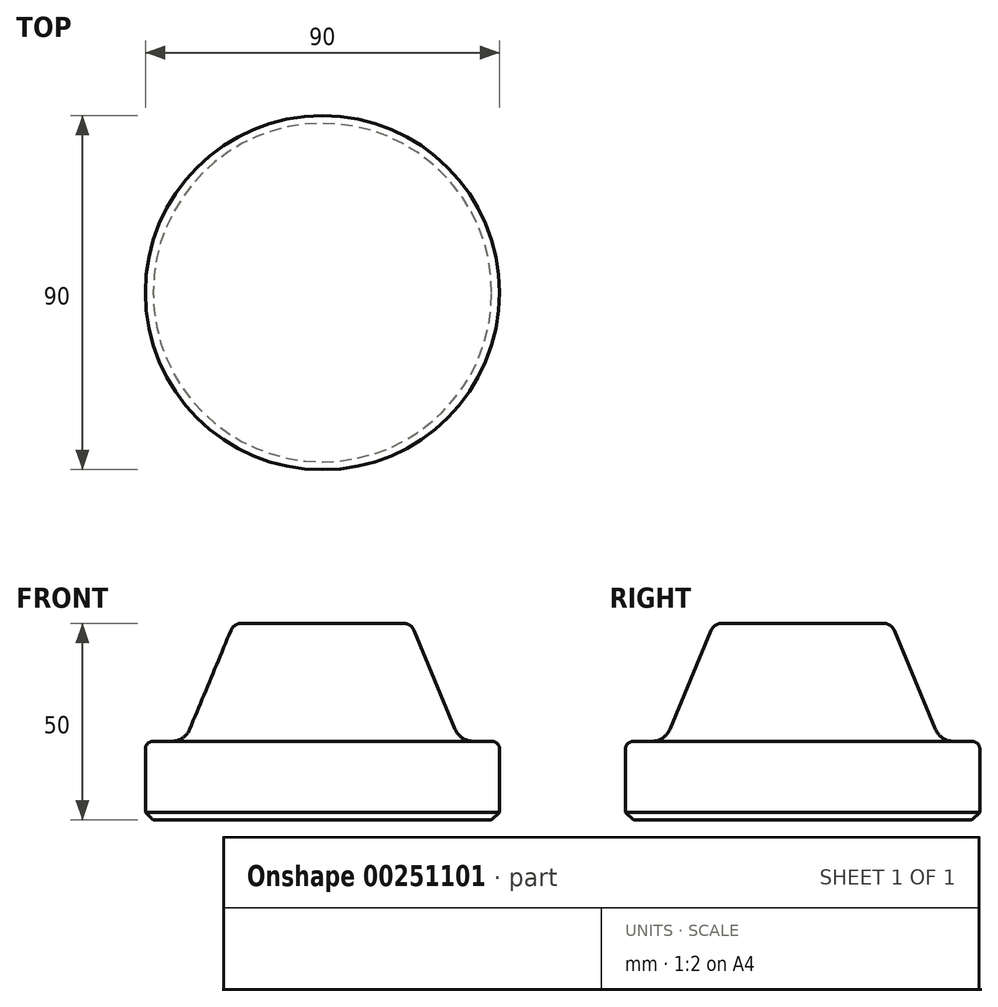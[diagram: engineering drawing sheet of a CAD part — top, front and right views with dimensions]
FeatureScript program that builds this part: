
annotation { "Feature Type Name" : "Feature", "Feature Type Description" : "" }
export const myFeature = defineFeature(function(context is Context, id is Id, definition is map)
    precondition{}
    {
        {
            var Q0;
            Q0=qCreatedBy(makeId("Front.planeOp"),FACE);
            var sketch = newSketch(context, id + "F0", { "sketchPlane" : qUnion([Q0])});
            skLineSegment(sketch, "E0", {"start": v(0, 50) * mm, "end": v(0, 0) * mm});
            skLineSegment(sketch, "E1", {"start": v(0, 0) * mm, "end": v(45, 0) * mm});
            skLineSegment(sketch, "E2", {"start": v(45, 0) * mm, "end": v(45, 18) * mm});
            skLineSegment(sketch, "E3", {"start": v(43, 20) * mm, "end": v(38.33, 20) * mm});
            skLineSegment(sketch, "E4", {"start": v(33.72, 23.08) * mm, "end": v(23.27, 48.15) * mm});
            skLineSegment(sketch, "E5", {"start": v(20.5, 50) * mm, "end": v(0, 50) * mm});
            skPoint(sketch, "E6.visualSharp", {"position": v(22.5, 50) * mm});
            skArc(sketch, "E6.filletArc", {"start": v(23.27, 48.15) * mm, "mid": v(22.16, 49.5) * mm, "end": v(20.5, 50) * mm});
            skPoint(sketch, "E7.visualSharp", {"position": v(35, 20) * mm});
            skArc(sketch, "E7.filletArc", {"start": v(33.72, 23.08) * mm, "mid": v(35.56, 20.84) * mm, "end": v(38.33, 20) * mm});
            skPoint(sketch, "E8.visualSharp", {"position": v(45, 20) * mm});
            skArc(sketch, "E8.filletArc", {"start": v(45, 18) * mm, "mid": v(44.41, 19.41) * mm, "end": v(43, 20) * mm});
            skLineSegment(sketch, "E9", {"start": v(0, -33.46) * mm, "end": v(0, 66.6) * mm, "construction": true});
            skSolve(sketch);
        }
        {
            var Q0;
            Q0=makeQuery(id+"F0.imprint","IMPRINT",FACE,{"disambiguationData":[TD([[makeQuery(id+"F0.imprint","IMPRINT",EDGE,{"derivedFrom":sQuery(id+"F0.wireOp",EDGE,"E0")}),1.0]])]});
            var Q1;
            Q1=sQuery(id+"F0.wireOp",EDGE,"E9");
            var Q2;
            Q2=sQuery(id+"F0.wireOp",EDGE,"E9");
            revolve(context, id + "F1", {"entities" : qUnion([Q0]), "surfaceEntities" : qUnion([Q1]), "axis" : qUnion([Q2]), "revolveType" : RevolveType.FULL});
        }
        {
            var Q0;
            Q0=makeQuery(id+"F1.opRevolve","SWEPT_EDGE",EDGE,{"disambiguationData":[OSD([sQuery(id+"F0.wireOp",EDGE,"E1"),sQuery(id+"F0.wireOp",EDGE,"E2")])]});
            chamfer(context, id + "F2", {"entities" : qUnion([Q0]), "width" : 2 * mm, "tangentPropagation" : true});
        }
    });
